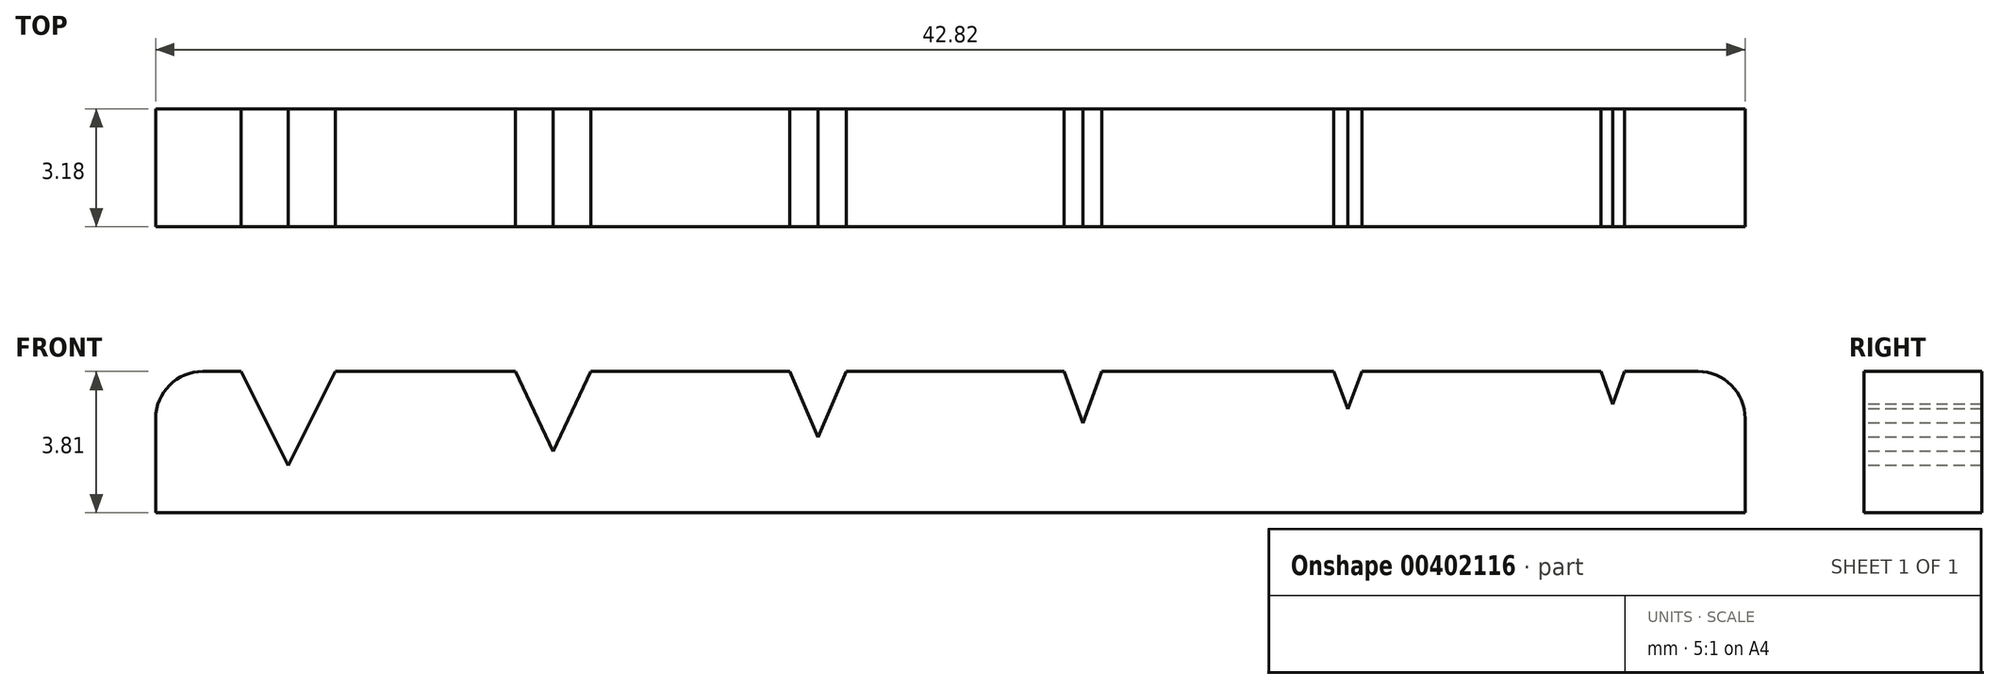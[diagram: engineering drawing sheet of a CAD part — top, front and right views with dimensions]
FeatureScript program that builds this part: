
annotation { "Feature Type Name" : "Feature", "Feature Type Description" : "" }
export const myFeature = defineFeature(function(context is Context, id is Id, definition is map)
    precondition{}
    {
        {
            var Q0;
            Q0=qCreatedBy(makeId("Top.planeOp"),FACE);
            var sketch = newSketch(context, id + "F0", { "sketchPlane" : qUnion([Q0])});
            skLineSegment(sketch, "E0.bottom", {"start": v(-21.41, 1.59) * mm, "end": v(21.41, 1.59) * mm});
            skLineSegment(sketch, "E0.top", {"start": v(-21.41, -1.59) * mm, "end": v(21.41, -1.59) * mm});
            skLineSegment(sketch, "E0.left", {"start": v(-21.41, 1.59) * mm, "end": v(-21.41, -1.59) * mm});
            skLineSegment(sketch, "E0.right", {"start": v(21.41, 1.59) * mm, "end": v(21.41, -1.59) * mm});
            skPoint(sketch, "E0.middle", {"position": v(0, 0) * mm});
            skLineSegment(sketch, "E1", {"start": v(-3.57, 1.59) * mm, "end": v(-3.57, -56.89) * mm, "construction": true});
            skLineSegment(sketch, "E2", {"start": v(3.57, 1.59) * mm, "end": v(3.57, -28.96) * mm, "construction": true});
            skLineSegment(sketch, "E3", {"start": v(0, 0) * mm, "end": v(0, -5.88) * mm, "construction": true});
            skPoint(sketch, "E3.endSnap0", {"position": v(0, -1.59) * mm});
            skLineSegment(sketch, "E4.1.0.0", {"start": v(10.7, 1.59) * mm, "end": v(10.7, -28.96) * mm, "construction": true});
            skLineSegment(sketch, "E4.2.0.0", {"start": v(17.84, 1.59) * mm, "end": v(17.84, -28.96) * mm, "construction": true});
            skLineSegment(sketch, "E4.direction1", {"start": v(3.57, -28.96) * mm, "end": v(10.7, -28.96) * mm, "construction": true});
            skLineSegment(sketch, "E5.1.0.0", {"start": v(-10.7, 1.59) * mm, "end": v(-10.7, -56.89) * mm, "construction": true});
            skLineSegment(sketch, "E5.2.0.0", {"start": v(-17.84, 1.59) * mm, "end": v(-17.84, -56.89) * mm, "construction": true});
            skLineSegment(sketch, "E5.direction1", {"start": v(-3.57, -56.89) * mm, "end": v(-10.7, -56.89) * mm, "construction": true});
            skSolve(sketch);
        }
        {
            var Q0;
            Q0=qSketchRegion(id+"F0",true);
            extrude(context, id + "F1", {"entities" : qUnion([Q0]), "oppositeDirection" : true, "depth" : 3.8 * mm});
        }
        {
            var Q0;
            Q0=makeQuery(id+"F1.opExtrude","SWEPT_FACE",FACE,{"disambiguationData":[OSD([sQuery(id+"F0.wireOp",EDGE,"E0.top")])]});
            var sketch = newSketch(context, id + "F2", { "sketchPlane" : qUnion([Q0])});
            skLineSegment(sketch, "E6", {"start": v(-19.11, 0) * mm, "end": v(-17.84, -2.54) * mm});
            skLineSegment(sketch, "E7", {"start": v(-17.84, -2.54) * mm, "end": v(-16.57, 0) * mm});
            skPoint(sketch, "E8", {"position": v(-17.84, -2.54) * mm});
            skPoint(sketch, "E9", {"position": v(-10.7, -2.54) * mm});
            skPoint(sketch, "E10.2.0.0", {"position": v(-3.57, -2.54) * mm});
            skPoint(sketch, "E10.3.0.0", {"position": v(3.57, -2.54) * mm});
            skPoint(sketch, "E10.4.0.0", {"position": v(10.7, -2.54) * mm});
            skPoint(sketch, "E10.5.0.0", {"position": v(17.84, -2.54) * mm});
            skLineSegment(sketch, "E10.direction1", {"start": v(-17.84, -2.54) * mm, "end": v(-10.7, -2.54) * mm, "construction": true});
            skLineSegment(sketch, "E11", {"start": v(-11.72, 0) * mm, "end": v(-10.7, -2.16) * mm});
            skLineSegment(sketch, "E12", {"start": v(-10.7, -2.16) * mm, "end": v(-9.69, 0) * mm});
            skLineSegment(sketch, "E13", {"start": v(-19.11, 0) * mm, "end": v(-16.57, 0) * mm});
            skLineSegment(sketch, "E14", {"start": v(-11.72, 0) * mm, "end": v(-9.69, 0) * mm});
            skLineSegment(sketch, "E15.1.0.0", {"start": v(-3.57, -1.78) * mm, "end": v(-2.8, 0) * mm});
            skLineSegment(sketch, "E15.1.0.1", {"start": v(-4.33, 0) * mm, "end": v(-3.57, -1.78) * mm});
            skLineSegment(sketch, "E15.1.0.2", {"start": v(-4.33, 0) * mm, "end": v(-2.8, 0) * mm});
            skLineSegment(sketch, "E15.2.0.0", {"start": v(3.57, -1.4) * mm, "end": v(4.08, 0) * mm});
            skLineSegment(sketch, "E15.2.0.1", {"start": v(3.06, 0) * mm, "end": v(3.57, -1.4) * mm});
            skLineSegment(sketch, "E15.2.0.2", {"start": v(3.06, 0) * mm, "end": v(4.08, 0) * mm});
            skLineSegment(sketch, "E15.3.0.0", {"start": v(10.7, -1.02) * mm, "end": v(11.09, 0) * mm});
            skLineSegment(sketch, "E15.3.0.1", {"start": v(10.32, 0) * mm, "end": v(10.7, -1.02) * mm});
            skLineSegment(sketch, "E15.3.0.2", {"start": v(10.32, 0) * mm, "end": v(11.09, 0) * mm});
            skLineSegment(sketch, "E15.4.0.0", {"start": v(17.84, -0.89) * mm, "end": v(18.16, 0) * mm});
            skLineSegment(sketch, "E15.4.0.1", {"start": v(17.52, 0) * mm, "end": v(17.84, -0.89) * mm});
            skLineSegment(sketch, "E15.4.0.2", {"start": v(17.52, 0) * mm, "end": v(18.16, 0) * mm});
            skSolve(sketch);
        }
        {
            var Q0;
            Q0=makeQuery(id+"F2.imprint","IMPRINT",FACE,{"disambiguationData":[TD([[makeQuery(id+"F2.imprint","IMPRINT",EDGE,{"derivedFrom":sQuery(id+"F2.wireOp",EDGE,"E6")}),1.0]])]});
            var Q1;
            Q1=makeQuery(id+"F2.imprint","IMPRINT",FACE,{"disambiguationData":[TD([[makeQuery(id+"F2.imprint","IMPRINT",EDGE,{"derivedFrom":sQuery(id+"F2.wireOp",EDGE,"E11")}),1.0]])]});
            var Q2;
            Q2=makeQuery(id+"F2.imprint","IMPRINT",FACE,{"disambiguationData":[TD([[makeQuery(id+"F2.imprint","IMPRINT",EDGE,{"derivedFrom":sQuery(id+"F2.wireOp",EDGE,"E15.1.0.0")}),1.0]])]});
            var Q3;
            Q3=makeQuery(id+"F2.imprint","IMPRINT",FACE,{"disambiguationData":[TD([[makeQuery(id+"F2.imprint","IMPRINT",EDGE,{"derivedFrom":sQuery(id+"F2.wireOp",EDGE,"E15.2.0.0")}),1.0]])]});
            var Q4;
            Q4=makeQuery(id+"F2.imprint","IMPRINT",FACE,{"disambiguationData":[TD([[makeQuery(id+"F2.imprint","IMPRINT",EDGE,{"derivedFrom":sQuery(id+"F2.wireOp",EDGE,"E15.3.0.0")}),1.0]])]});
            var Q5;
            Q5=makeQuery(id+"F2.imprint","IMPRINT",FACE,{"disambiguationData":[TD([[makeQuery(id+"F2.imprint","IMPRINT",EDGE,{"derivedFrom":sQuery(id+"F2.wireOp",EDGE,"E15.4.0.0")}),1.0]])]});
            extrude(context, id + "F3", {"entities" : qUnion([Q0, Q1, Q2, Q3, Q4, Q5]), "operationType" : NewBodyOperationType.REMOVE, "endBound" : BoundingType.THROUGH_ALL, "oppositeDirection" : true, "depth" : 25.4 * mm});
        }
        {
            var Q0;
            Q0=makeQuery(id+"F1.opExtrude","CAP_EDGE",EDGE,{"disambiguationData":[OSD([sQuery(id+"F0.wireOp",EDGE,"E0.left")])],"isStart":true});
            var Q1;
            Q1=makeQuery(id+"F1.opExtrude","CAP_EDGE",EDGE,{"disambiguationData":[OSD([sQuery(id+"F0.wireOp",EDGE,"E0.right")])],"isStart":true});
            fillet(context, id + "F4", {"entities" : qUnion([Q0, Q1]), "radius" : 1.27 * mm, "tangentPropagation" : true, "allowEdgeOverflow" : false});
        }
    });
